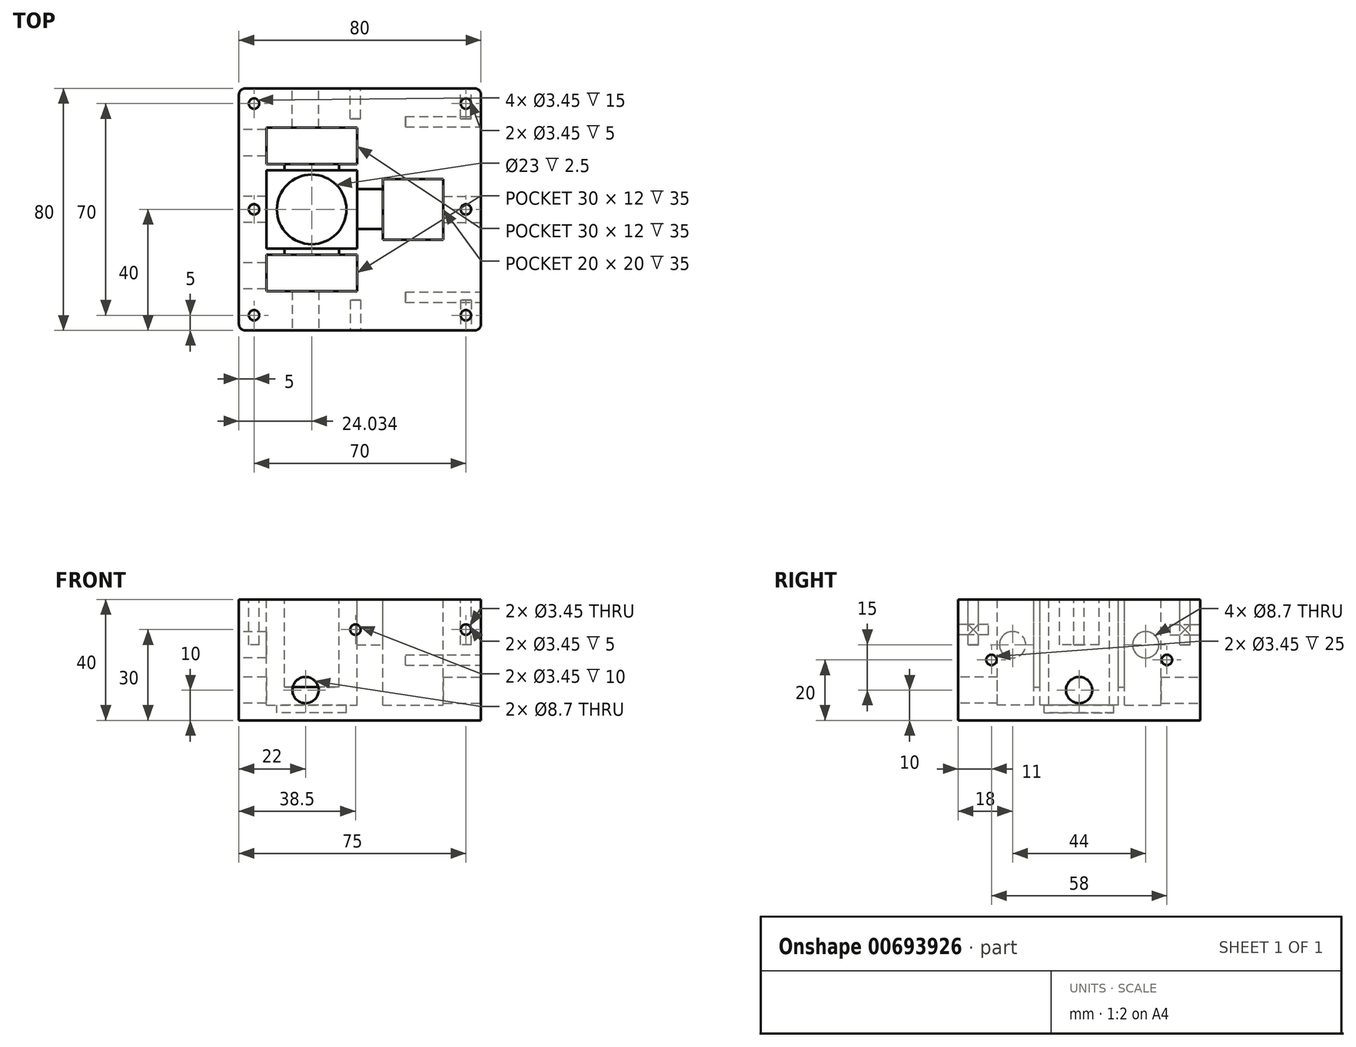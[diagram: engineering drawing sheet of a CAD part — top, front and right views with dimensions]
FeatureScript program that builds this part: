
annotation { "Feature Type Name" : "Feature", "Feature Type Description" : "" }
export const myFeature = defineFeature(function(context is Context, id is Id, definition is map)
    precondition{}
    {
        {
            var Q0;
            Q0=qCreatedBy(makeId("Top.planeOp"),FACE);
            var sketch = newSketch(context, id + "F0", { "sketchPlane" : qUnion([Q0])});
            skLineSegment(sketch, "E0.bottom", {"start": v(38, 40) * mm, "end": v(-38, 40) * mm});
            skLineSegment(sketch, "E0.top", {"start": v(38, -40) * mm, "end": v(-38, -40) * mm});
            skLineSegment(sketch, "E0.left", {"start": v(40, 38) * mm, "end": v(40, -38) * mm});
            skLineSegment(sketch, "E0.right", {"start": v(-40, 38) * mm, "end": v(-40, -38) * mm});
            skPoint(sketch, "E0.middle", {"position": v(0, 0) * mm});
            skPoint(sketch, "E1.visualSharp", {"position": v(-40, 40) * mm});
            skArc(sketch, "E1.filletArc", {"start": v(-38, 40) * mm, "mid": v(-39.41, 39.41) * mm, "end": v(-40, 38) * mm});
            skPoint(sketch, "E2.visualSharp", {"position": v(40, 40) * mm});
            skArc(sketch, "E2.filletArc", {"start": v(40, 38) * mm, "mid": v(39.41, 39.41) * mm, "end": v(38, 40) * mm});
            skPoint(sketch, "E3.visualSharp", {"position": v(40, -40) * mm});
            skArc(sketch, "E3.filletArc", {"start": v(38, -40) * mm, "mid": v(39.41, -39.41) * mm, "end": v(40, -38) * mm});
            skPoint(sketch, "E4.visualSharp", {"position": v(-40, -40) * mm});
            skArc(sketch, "E4.filletArc", {"start": v(-40, -38) * mm, "mid": v(-39.41, -39.41) * mm, "end": v(-38, -40) * mm});
            skSolve(sketch);
        }
        {
            var Q0;
            Q0 = qSketchRegion(id + "F0", true);
            extrude(context, id + "F1", {"entities" : qUnion([Q0]), "depth" : 40 * mm, "offsetDistance" : 25 * mm});
        }
        {
            var Q0;
            Q0=makeQuery(id+"F1.opExtrude","CAP_FACE",FACE,{"disambiguationData":[OSD([sQuery(id+"F0.wireOp",EDGE,"E0.bottom"),sQuery(id+"F0.wireOp",EDGE,"E0.top"),sQuery(id+"F0.wireOp",EDGE,"E0.left"),sQuery(id+"F0.wireOp",EDGE,"E0.right"),sQuery(id+"F0.wireOp",EDGE,"E1.filletArc"),sQuery(id+"F0.wireOp",EDGE,"E2.filletArc"),sQuery(id+"F0.wireOp",EDGE,"E3.filletArc"),sQuery(id+"F0.wireOp",EDGE,"E4.filletArc")])],"isStart":false});
            var sketch = newSketch(context, id + "F2", { "sketchPlane" : qUnion([Q0])});
            skPoint(sketch, "E5.middle", {"position": v(0, 0) * mm});
            skLineSegment(sketch, "E6.bottom", {"start": v(7.5, 10) * mm, "end": v(27.5, 10) * mm});
            skLineSegment(sketch, "E6.top", {"start": v(7.5, -10) * mm, "end": v(27.5, -10) * mm});
            skLineSegment(sketch, "E6.left", {"start": v(7.5, 10) * mm, "end": v(7.5, -10) * mm});
            skLineSegment(sketch, "E6.right", {"start": v(27.5, 10) * mm, "end": v(27.5, -10) * mm});
            skPoint(sketch, "E6.middle", {"position": v(17.5, 0) * mm});
            skPoint(sketch, "E7.middle", {"position": v(-15.97, 0) * mm});
            skLineSegment(sketch, "E8", {"start": v(-30.97, -15) * mm, "end": v(-30.97, -27) * mm});
            skLineSegment(sketch, "E9", {"start": v(-0.97, -27) * mm, "end": v(-0.97, -15) * mm});
            skLineSegment(sketch, "E10.bottom", {"start": v(-30.97, 13) * mm, "end": v(-24.97, 13) * mm});
            skLineSegment(sketch, "E10.top", {"start": v(-30.97, 15) * mm, "end": v(-24.97, 15) * mm});
            skLineSegment(sketch, "E10.right", {"start": v(-24.97, 13) * mm, "end": v(-24.97, 15) * mm});
            skLineSegment(sketch, "E11.bottom", {"start": v(-0.97, 13) * mm, "end": v(-6.97, 13) * mm});
            skLineSegment(sketch, "E11.top", {"start": v(-0.97, 15) * mm, "end": v(-6.97, 15) * mm});
            skLineSegment(sketch, "E11.right", {"start": v(-6.97, 13) * mm, "end": v(-6.97, 15) * mm});
            skLineSegment(sketch, "E12.bottom", {"start": v(-30.97, -15) * mm, "end": v(-24.97, -15) * mm});
            skLineSegment(sketch, "E12.top", {"start": v(-30.97, -13) * mm, "end": v(-24.97, -13) * mm});
            skLineSegment(sketch, "E12.right", {"start": v(-24.97, -15) * mm, "end": v(-24.97, -13) * mm});
            skLineSegment(sketch, "E13.bottom", {"start": v(-0.97, -15) * mm, "end": v(-6.97, -15) * mm});
            skLineSegment(sketch, "E13.top", {"start": v(-0.97, -13) * mm, "end": v(-6.97, -13) * mm});
            skLineSegment(sketch, "E13.right", {"start": v(-6.97, -15) * mm, "end": v(-6.97, -13) * mm});
            skLineSegment(sketch, "E14", {"start": v(-30.97, 15) * mm, "end": v(-30.97, 27) * mm});
            skLineSegment(sketch, "E15", {"start": v(-0.97, 15) * mm, "end": v(-0.97, 27) * mm});
            skLineSegment(sketch, "E16", {"start": v(-30.97, -27) * mm, "end": v(-0.97, -27) * mm});
            skLineSegment(sketch, "E17", {"start": v(-30.97, 27) * mm, "end": v(-0.97, 27) * mm});
            skLineSegment(sketch, "E18", {"start": v(-30.97, 13) * mm, "end": v(-30.97, -13) * mm});
            skLineSegment(sketch, "E19", {"start": v(-0.97, 13) * mm, "end": v(-0.97, -13) * mm});
            skLineSegment(sketch, "E20", {"start": v(-30.97, 0) * mm, "end": v(-15.97, 0) * mm, "construction": true});
            skLineSegment(sketch, "E21", {"start": v(-15.97, 0) * mm, "end": v(-0.97, 0) * mm, "construction": true});
            skSolve(sketch);
        }
        {
            var Q0;
            Q0 = qSketchRegion(id + "F2", true);
            extrude(context, id + "F3", {"entities" : qUnion([Q0]), "operationType" : NewBodyOperationType.REMOVE, "oppositeDirection" : true, "depth" : 35 * mm, "offsetDistance" : 25 * mm});
        }
        {
            var Q0;
            Q0=makeQuery(id+"F1.opExtrude","SWEPT_FACE",FACE,{"disambiguationData":[OSD([sQuery(id+"F0.wireOp",EDGE,"E0.right")])]});
            var sketch = newSketch(context, id + "F4", { "sketchPlane" : qUnion([Q0])});
            skCircle(sketch, "E22", {"center": v(-22, 25) * mm, "radius": 4.35 * mm});
            skLineSegment(sketch, "E23", {"start": v(-22, 40) * mm, "end": v(-22, 0) * mm, "construction": true});
            skLineSegment(sketch, "E24", {"start": v(22, 40) * mm, "end": v(22, 0) * mm, "construction": true});
            skLineSegment(sketch, "E25", {"start": v(-38, 25) * mm, "end": v(38, 25) * mm, "construction": true});
            skLineSegment(sketch, "E26", {"start": v(-38, 10) * mm, "end": v(38, 10) * mm, "construction": true});
            skPoint(sketch, "E27", {"position": v(-22, 20) * mm});
            skCircle(sketch, "E28", {"center": v(22, 25) * mm, "radius": 4.35 * mm});
            skCircle(sketch, "E29", {"center": v(0, 10) * mm, "radius": 4.35 * mm});
            skSolve(sketch);
        }
        {
            var Q0;
            Q0 = qSketchRegion(id + "F4", true);
            extrude(context, id + "F5", {"entities" : qUnion([Q0]), "operationType" : NewBodyOperationType.REMOVE, "oppositeDirection" : true, "depth" : 15 * mm, "offsetDistance" : 25 * mm});
        }
        {
            var Q0;
            Q0=makeQuery(id+"F1.opExtrude","SWEPT_FACE",FACE,{"disambiguationData":[OSD([sQuery(id+"F0.wireOp",EDGE,"E0.left")])]});
            var sketch = newSketch(context, id + "F6", { "sketchPlane" : qUnion([Q0])});
            skCircle(sketch, "E30", {"center": v(0, 10) * mm, "radius": 4.35 * mm});
            skLineSegment(sketch, "E31", {"start": v(-38, 10) * mm, "end": v(38, 10) * mm, "construction": true});
            skSolve(sketch);
        }
        {
            var Q0;
            Q0=makeQuery(id+"F6.imprint","IMPRINT",FACE,{"disambiguationData":[TD([[makeQuery(id+"F6.imprint","IMPRINT",EDGE,{"derivedFrom":sQuery(id+"F6.wireOp",EDGE,"E30")}),1.0]])]});
            extrude(context, id + "F7", {"entities" : qUnion([Q0]), "operationType" : NewBodyOperationType.REMOVE, "oppositeDirection" : true, "depth" : 15 * mm, "offsetDistance" : 25 * mm});
        }
        {
            var Q0;
            Q0=makeQuery(id+"F1.opExtrude","CAP_FACE",FACE,{"disambiguationData":[OSD([sQuery(id+"F0.wireOp",EDGE,"E0.bottom"),sQuery(id+"F0.wireOp",EDGE,"E0.top"),sQuery(id+"F0.wireOp",EDGE,"E0.left"),sQuery(id+"F0.wireOp",EDGE,"E0.right"),sQuery(id+"F0.wireOp",EDGE,"E1.filletArc"),sQuery(id+"F0.wireOp",EDGE,"E2.filletArc"),sQuery(id+"F0.wireOp",EDGE,"E3.filletArc"),sQuery(id+"F0.wireOp",EDGE,"E4.filletArc")])],"isStart":false});
            var sketch = newSketch(context, id + "F8", { "sketchPlane" : qUnion([Q0])});
            skLineSegment(sketch, "E32.bottom", {"start": v(-0.97, -6.5) * mm, "end": v(7.5, -6.5) * mm});
            skLineSegment(sketch, "E32.top", {"start": v(-0.97, 6.67) * mm, "end": v(7.5, 6.67) * mm});
            skLineSegment(sketch, "E32.left", {"start": v(-0.97, -6.5) * mm, "end": v(-0.97, 6.67) * mm});
            skLineSegment(sketch, "E32.right", {"start": v(7.5, -6.5) * mm, "end": v(7.5, 6.67) * mm});
            skSolve(sketch);
        }
        {
            var Q0;
            Q0 = qSketchRegion(id + "F8", true);
            extrude(context, id + "F9", {"entities" : qUnion([Q0]), "operationType" : NewBodyOperationType.REMOVE, "oppositeDirection" : true, "depth" : 15 * mm, "offsetDistance" : 25 * mm});
        }
        {
            var Q0;
            Q0=makeQuery(id+"F1.opExtrude","CAP_FACE",FACE,{"disambiguationData":[OSD([sQuery(id+"F0.wireOp",EDGE,"E0.bottom"),sQuery(id+"F0.wireOp",EDGE,"E0.top"),sQuery(id+"F0.wireOp",EDGE,"E0.left"),sQuery(id+"F0.wireOp",EDGE,"E0.right"),sQuery(id+"F0.wireOp",EDGE,"E1.filletArc"),sQuery(id+"F0.wireOp",EDGE,"E2.filletArc"),sQuery(id+"F0.wireOp",EDGE,"E3.filletArc"),sQuery(id+"F0.wireOp",EDGE,"E4.filletArc")])],"isStart":false});
            var sketch = newSketch(context, id + "F10", { "sketchPlane" : qUnion([Q0])});
            skCircle(sketch, "E33", {"center": v(-35, 0) * mm, "radius": 1.72 * mm});
            skLineSegment(sketch, "E34", {"start": v(-40, 0) * mm, "end": v(40, 0) * mm, "construction": true});
            skCircle(sketch, "E35", {"center": v(35, 0) * mm, "radius": 1.72 * mm});
            skLineSegment(sketch, "E36", {"start": v(-35, 0) * mm, "end": v(-35, 40) * mm, "construction": true});
            skLineSegment(sketch, "E37", {"start": v(-35, 0) * mm, "end": v(-35, -40) * mm, "construction": true});
            skLineSegment(sketch, "E38", {"start": v(35, 0) * mm, "end": v(35, 40) * mm, "construction": true});
            skLineSegment(sketch, "E39", {"start": v(35, 0) * mm, "end": v(35, -40) * mm, "construction": true});
            skCircle(sketch, "E40", {"center": v(-35, 35) * mm, "radius": 1.73 * mm});
            skCircle(sketch, "E41", {"center": v(-35, -35) * mm, "radius": 1.73 * mm});
            skCircle(sketch, "E42", {"center": v(35, 35) * mm, "radius": 1.73 * mm});
            skCircle(sketch, "E43", {"center": v(35, -35) * mm, "radius": 1.73 * mm});
            skSolve(sketch);
        }
        {
            var Q0;
            Q0 = qSketchRegion(id + "F10", true);
            extrude(context, id + "F11", {"entities" : qUnion([Q0]), "operationType" : NewBodyOperationType.REMOVE, "oppositeDirection" : true, "depth" : 15 * mm, "offsetDistance" : 25 * mm});
        }
        {
            var Q0;
            Q0=makeQuery(id+"F3.boolean.opBoolean","COPY",FACE,{"derivedFrom":makeQuery(id+"F3.opExtrude","CAP_FACE",FACE,{"disambiguationData":[OSD([sQuery(id+"F2.wireOp",EDGE,"E8"),sQuery(id+"F2.wireOp",EDGE,"E9"),sQuery(id+"F2.wireOp",EDGE,"E10.bottom"),sQuery(id+"F2.wireOp",EDGE,"E10.top"),sQuery(id+"F2.wireOp",EDGE,"E10.right"),sQuery(id+"F2.wireOp",EDGE,"E11.bottom"),sQuery(id+"F2.wireOp",EDGE,"E11.top"),sQuery(id+"F2.wireOp",EDGE,"E11.right"),sQuery(id+"F2.wireOp",EDGE,"E12.bottom"),sQuery(id+"F2.wireOp",EDGE,"E12.top"),sQuery(id+"F2.wireOp",EDGE,"E12.right"),sQuery(id+"F2.wireOp",EDGE,"E13.bottom"),sQuery(id+"F2.wireOp",EDGE,"E13.top"),sQuery(id+"F2.wireOp",EDGE,"E13.right"),sQuery(id+"F2.wireOp",EDGE,"E14"),sQuery(id+"F2.wireOp",EDGE,"E15"),sQuery(id+"F2.wireOp",EDGE,"E16"),sQuery(id+"F2.wireOp",EDGE,"E17"),sQuery(id+"F2.wireOp",EDGE,"E18"),sQuery(id+"F2.wireOp",EDGE,"E19")])],"isStart":false})});
            var sketch = newSketch(context, id + "F12", { "sketchPlane" : qUnion([Q0])});
            skCircle(sketch, "E44", {"center": v(-15.97, 0) * mm, "radius": 11.5 * mm});
            skLineSegment(sketch, "E45", {"start": v(-15.97, 27) * mm, "end": v(-15.97, 0) * mm, "construction": true});
            skLineSegment(sketch, "E46", {"start": v(-15.97, 0) * mm, "end": v(-15.97, -27) * mm, "construction": true});
            skSolve(sketch);
        }
        {
            var Q0;
            Q0=makeQuery(id+"F12.imprint","IMPRINT",FACE,{"disambiguationData":[TD([[makeQuery(id+"F12.imprint","IMPRINT",EDGE,{"derivedFrom":sQuery(id+"F12.wireOp",EDGE,"bb912ac5-35b0-4ee9-8634-8bc003714958.bottom")}),-1.0]])]});
            var Q1;
            Q1=makeQuery(id+"F12.imprint","IMPRINT",FACE,{"disambiguationData":[TD([[makeQuery(id+"F12.imprint","IMPRINT",EDGE,{"derivedFrom":sQuery(id+"F12.wireOp",EDGE,"E44")}),1.0]])]});
            var Q2;
            Q2=makeQuery(id+"F12.imprint","IMPRINT",FACE,{"disambiguationData":[TD([[makeQuery(id+"F12.imprint","IMPRINT",EDGE,{"derivedFrom":sQuery(id+"F12.wireOp",EDGE,"gYT2ciQ3-SqBT-WjhR-Vjhe-1WiG50xRSuUY.bottom")}),-1.0]])]});
            var Q3;
            Q3=makeQuery(id+"F12.imprint","IMPRINT",FACE,{"disambiguationData":[TD([[makeQuery(id+"F12.imprint","IMPRINT",EDGE,{"derivedFrom":sQuery(id+"F12.wireOp",EDGE,"g5Y9EQOG-34RZ-q3BQ-wkZC-m2n6YxgDQQkI.top")}),-1.0]])]});
            var Q4;
            Q4=makeQuery(id+"F12.imprint","IMPRINT",FACE,{"disambiguationData":[TD([[makeQuery(id+"F12.imprint","IMPRINT",EDGE,{"derivedFrom":sQuery(id+"F12.wireOp",EDGE,"yKDrHwcH-aapL-mzDN-iYDB-Ey4W7c4Ljunm.top")}),1.0]])]});
            extrude(context, id + "F13", {"entities" : qUnion([Q0, Q1, Q2, Q3, Q4]), "operationType" : NewBodyOperationType.REMOVE, "oppositeDirection" : true, "depth" : 2.5 * mm, "offsetDistance" : 25 * mm});
        }
        {
            var Q0;
            Q0=makeQuery(id+"F1.opExtrude","SWEPT_FACE",FACE,{"disambiguationData":[OSD([sQuery(id+"F0.wireOp",EDGE,"E0.top")])]});
            var sketch = newSketch(context, id + "F14", { "sketchPlane" : qUnion([Q0])});
            skCircle(sketch, "E47", {"center": v(-1.5, 30) * mm, "radius": 1.73 * mm});
            skCircle(sketch, "E48", {"center": v(35, 30) * mm, "radius": 1.73 * mm});
            skSolve(sketch);
        }
        {
            var Q0;
            Q0 = qSketchRegion(id + "F14", true);
            extrude(context, id + "F15", {"entities" : qUnion([Q0]), "operationType" : NewBodyOperationType.REMOVE, "oppositeDirection" : true, "depth" : 10 * mm, "offsetDistance" : 25 * mm});
        }
        {
            var Q0;
            Q0=makeQuery(id+"F1.opExtrude","SWEPT_FACE",FACE,{"disambiguationData":[OSD([sQuery(id+"F0.wireOp",EDGE,"E0.bottom")])]});
            var sketch = newSketch(context, id + "F16", { "sketchPlane" : qUnion([Q0])});
            skCircle(sketch, "E49", {"center": v(-35, 30) * mm, "radius": 1.73 * mm});
            skCircle(sketch, "E50", {"center": v(1.5, 30) * mm, "radius": 1.73 * mm});
            skSolve(sketch);
        }
        {
            var Q0;
            Q0 = qSketchRegion(id + "F16", true);
            extrude(context, id + "F17", {"entities" : qUnion([Q0]), "operationType" : NewBodyOperationType.REMOVE, "oppositeDirection" : true, "depth" : 10 * mm, "offsetDistance" : 25 * mm});
        }
        {
            var Q0;
            Q0=makeQuery(id+"F1.opExtrude","SWEPT_FACE",FACE,{"disambiguationData":[OSD([sQuery(id+"F0.wireOp",EDGE,"E0.left")])]});
            var sketch = newSketch(context, id + "F18", { "sketchPlane" : qUnion([Q0])});
            skLineSegment(sketch, "E51", {"start": v(-38, 20) * mm, "end": v(38, 20) * mm, "construction": true});
            skCircle(sketch, "E52", {"center": v(-29, 20) * mm, "radius": 1.73 * mm});
            skCircle(sketch, "E53", {"center": v(29, 20) * mm, "radius": 1.73 * mm});
            skSolve(sketch);
        }
        {
            var Q0;
            Q0 = qSketchRegion(id + "F18", true);
            extrude(context, id + "F19", {"entities" : qUnion([Q0]), "operationType" : NewBodyOperationType.REMOVE, "oppositeDirection" : true, "depth" : 25 * mm, "offsetDistance" : 25 * mm});
        }
        {
            var Q0;
            Q0=makeQuery(id+"F1.opExtrude","SWEPT_FACE",FACE,{"disambiguationData":[OSD([sQuery(id+"F0.wireOp",EDGE,"E0.bottom")])]});
            var sketch = newSketch(context, id + "F20", { "sketchPlane" : qUnion([Q0])});
            skLineSegment(sketch, "E54", {"start": v(-38, 10) * mm, "end": v(38, 10) * mm, "construction": true});
            skCircle(sketch, "E55", {"center": v(18, 10) * mm, "radius": 4.35 * mm});
            skSolve(sketch);
        }
        {
            var Q0;
            Q0 = qSketchRegion(id + "F20", true);
            extrude(context, id + "F21", {"entities" : qUnion([Q0]), "operationType" : NewBodyOperationType.REMOVE, "oppositeDirection" : true, "depth" : 15 * mm, "offsetDistance" : 25 * mm});
        }
        {
            var Q0;
            Q0=makeQuery(id+"F1.opExtrude","SWEPT_FACE",FACE,{"disambiguationData":[OSD([sQuery(id+"F0.wireOp",EDGE,"E0.top")])]});
            var sketch = newSketch(context, id + "F22", { "sketchPlane" : qUnion([Q0])});
            skLineSegment(sketch, "E56", {"start": v(-38, 10) * mm, "end": v(38, 10) * mm, "construction": true});
            skCircle(sketch, "E57", {"center": v(-18, 10) * mm, "radius": 4.35 * mm});
            skSolve(sketch);
        }
        {
            var Q0;
            Q0 = qSketchRegion(id + "F22", true);
            extrude(context, id + "F23", {"entities" : qUnion([Q0]), "operationType" : NewBodyOperationType.REMOVE, "oppositeDirection" : true, "depth" : 15 * mm, "offsetDistance" : 25 * mm});
        }
        {
            var Q0;
            Q0=makeQuery(id+"F3.boolean.opBoolean","COPY",FACE,{"derivedFrom":makeQuery(id+"F3.opExtrude","CAP_FACE",FACE,{"disambiguationData":[OSD([sQuery(id+"F2.wireOp",EDGE,"Qd6BcOAe-JTxG-NwlI-p6aJ-pFO4ms3x8aWA"),sQuery(id+"F2.wireOp",EDGE,"3tzLtu1Z-8oIh-qoAj-xatf-JuWI9WQxj9eH"),sQuery(id+"F2.wireOp",EDGE,"zboivL9C-BZz7-vYwg-WIi6-ong4gXngRwuk"),sQuery(id+"F2.wireOp",EDGE,"E8"),sQuery(id+"F2.wireOp",EDGE,"EGl91Dpw-Fmb8-3Ufy-GdQk-a7yZQkEI3Jls"),sQuery(id+"F2.wireOp",EDGE,"mPXOd9YS-cYcO-yRTB-tOrx-fdxKp1V1F0JY"),sQuery(id+"F2.wireOp",EDGE,"E9"),sQuery(id+"F2.wireOp",EDGE,"oGzkXiVr-pozM-HoAo-wbEb-b7OAMStW5DZC"),sQuery(id+"F2.wireOp",EDGE,"E10.bottom"),sQuery(id+"F2.wireOp",EDGE,"E10.top"),sQuery(id+"F2.wireOp",EDGE,"E10.right"),sQuery(id+"F2.wireOp",EDGE,"E11.bottom"),sQuery(id+"F2.wireOp",EDGE,"E11.top"),sQuery(id+"F2.wireOp",EDGE,"E11.right"),sQuery(id+"F2.wireOp",EDGE,"E12.bottom"),sQuery(id+"F2.wireOp",EDGE,"E12.top"),sQuery(id+"F2.wireOp",EDGE,"E12.right"),sQuery(id+"F2.wireOp",EDGE,"E13.bottom"),sQuery(id+"F2.wireOp",EDGE,"E13.top"),sQuery(id+"F2.wireOp",EDGE,"E13.right"),sQuery(id+"F2.wireOp",EDGE,"E14"),sQuery(id+"F2.wireOp",EDGE,"E15"),sQuery(id+"F2.wireOp",EDGE,"x6izW37g-ivRo-a0nq-tskl-vGYnuKupSrzk"),sQuery(id+"F2.wireOp",EDGE,"JvyIWs5i-YAx6-vk8U-N7vB-Wef6Aw1g0a1F"),sQuery(id+"F2.wireOp",EDGE,"0MRyQDLE-ChKb-c5yb-5N0A-0X6oLUlssHQF"),sQuery(id+"F2.wireOp",EDGE,"f5bW3G8E-HI9G-yeK6-gerS-UGVSzlHJmsnx")])],"isStart":false})});
            var sketch = newSketch(context, id + "F24", { "sketchPlane" : qUnion([Q0])});
            skLineSegment(sketch, "E58", {"start": v(-24.97, 15) * mm, "end": v(-6.97, 15) * mm});
            skLineSegment(sketch, "E59", {"start": v(-6.97, 15) * mm, "end": v(-6.97, 13) * mm});
            skLineSegment(sketch, "E60", {"start": v(-6.97, 13) * mm, "end": v(-24.97, 13) * mm});
            skLineSegment(sketch, "E61", {"start": v(-24.97, 13) * mm, "end": v(-24.97, 15) * mm});
            skLineSegment(sketch, "E62", {"start": v(-24.97, -13) * mm, "end": v(-6.97, -13) * mm});
            skLineSegment(sketch, "E63", {"start": v(-6.97, -13) * mm, "end": v(-6.97, -15) * mm});
            skLineSegment(sketch, "E64", {"start": v(-6.97, -15) * mm, "end": v(-24.97, -15) * mm});
            skLineSegment(sketch, "E65", {"start": v(-24.97, -15) * mm, "end": v(-24.97, -13) * mm});
            skSolve(sketch);
        }
        {
            var Q0;
            Q0 = qSketchRegion(id + "F24", true);
            extrude(context, id + "F25", {"entities" : qUnion([Q0]), "operationType" : NewBodyOperationType.ADD, "depth" : 6 * mm, "offsetDistance" : 25 * mm});
        }
    });
